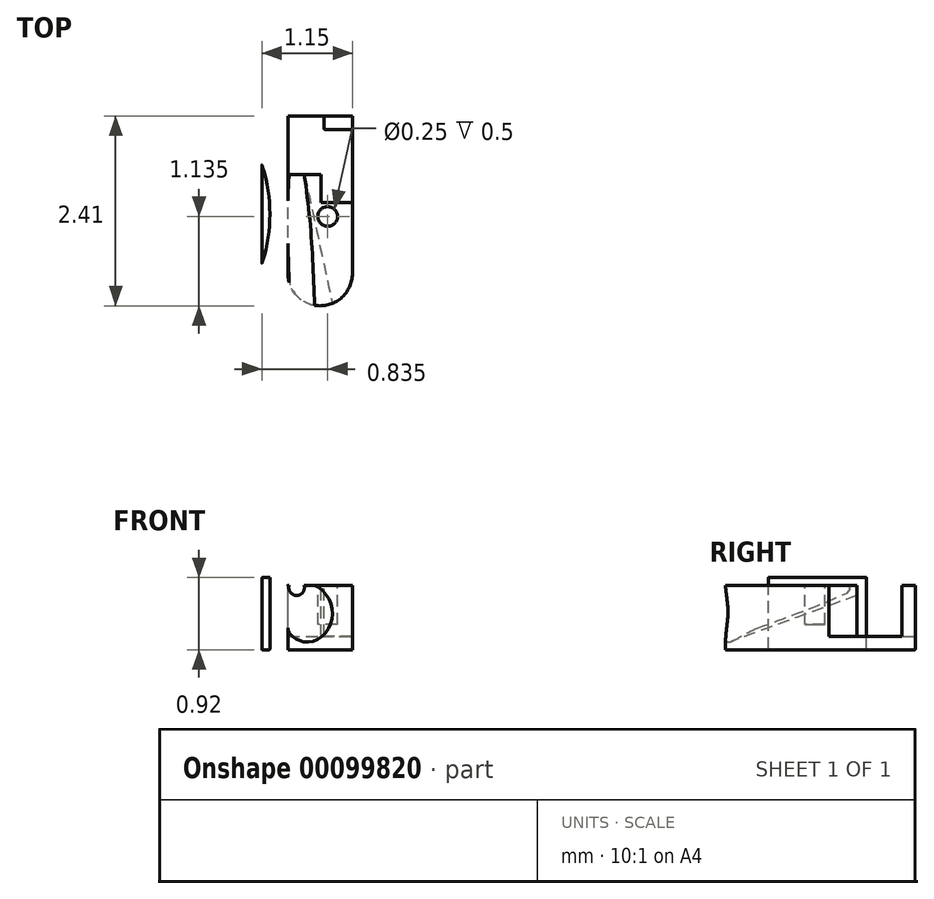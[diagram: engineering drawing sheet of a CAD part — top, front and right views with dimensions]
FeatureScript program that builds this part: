
annotation { "Feature Type Name" : "Feature", "Feature Type Description" : "" }
export const myFeature = defineFeature(function(context is Context, id is Id, definition is map)
    precondition{}
    {
        {
            var Q0;
            Q0=qCreatedBy(makeId("Front.planeOp"),FACE);
            var sketch = newSketch(context, id + "F0", { "sketchPlane" : qUnion([Q0])});
            skLineSegment(sketch, "E0", {"start": v(0, 0) * mm, "end": v(0.71, 0) * mm});
            skLineSegment(sketch, "E1", {"start": v(0.71, 0) * mm, "end": v(0.71, 0.92) * mm});
            skLineSegment(sketch, "E2", {"start": v(0.71, 0.92) * mm, "end": v(0, 0.92) * mm});
            skLineSegment(sketch, "E3.MirrorCS", {"start": v(-0.71, 0.92) * mm, "end": v(0, 0.92) * mm});
            skLineSegment(sketch, "E4.MirrorCS", {"start": v(-0.71, 0) * mm, "end": v(-0.71, 0.92) * mm});
            skLineSegment(sketch, "E5.MirrorCS", {"start": v(0, 0) * mm, "end": v(-0.71, 0) * mm});
            skSolve(sketch);
        }
        {
            var Q0;
            Q0 = qSketchRegion(id + "F0", true);
            var Q1;
            Q1=makeQuery(id+"F0.imprint","IMPRINT",FACE,{"disambiguationData":[TD([[makeQuery(id+"F0.imprint","IMPRINT",EDGE,{"derivedFrom":sQuery(id+"F0.wireOp",EDGE,"E0")}),1.0]])]});
            extrude(context, id + "F1", {"entities" : qUnion([Q0, Q1]), "oppositeDirection" : true, "depth" : 2.5 * mm});
        }
        {
            var Q0;
            Q0=qCreatedBy(makeId("Front.planeOp"),FACE);
            cPlane(context, id + "F2", {"entities" : qUnion([Q0]), "cplaneType" : CPlaneType.OFFSET, "offset" : 1.75 * mm, "oppositeDirection" : true, "width" : 150 * mm, "height" : 150 * mm});
        }
        {
            var Q0;
            Q0=qCreatedBy(id+"F2.planeOp",FACE);
            var sketch = newSketch(context, id + "F3", { "sketchPlane" : qUnion([Q0])});
            skCircle(sketch, "E6", {"center": v(-0.27, 0.79) * mm, "radius": 0.1 * mm});
            skSolve(sketch);
        }
        {
            var Q0;
            Q0=makeQuery(id+"F1.opExtrude","CAP_FACE",FACE,{"disambiguationData":[OSD([sQuery(id+"F0.wireOp",EDGE,"E0"),sQuery(id+"F0.wireOp",EDGE,"E1"),sQuery(id+"F0.wireOp",EDGE,"E2"),sQuery(id+"F0.wireOp",EDGE,"E3.MirrorCS"),sQuery(id+"F0.wireOp",EDGE,"E4.MirrorCS"),sQuery(id+"F0.wireOp",EDGE,"E5.MirrorCS")])],"isStart":true});
            var sketch = newSketch(context, id + "F4", { "sketchPlane" : qUnion([Q0])});
            skCircle(sketch, "E7", {"center": v(-0.2, 0.45) * mm, "radius": 0.4 * mm});
            skSolve(sketch);
        }
        {
            var Q1;
            Q1 = qSketchRegion(id + "F4", true);
            var Q2;
            Q2 = qSketchRegion(id + "F3", true);
            loft(context, id + "F5", {"operationType" : NewBodyOperationType.REMOVE, "sheetProfilesArray" : [{ "sheetProfileEntities" : qUnion([Q1]) }, { "sheetProfileEntities" : qUnion([Q2]) }]});
        }
        {
            var Q0;
            Q0=makeQuery(id+"F1.opExtrude","SWEPT_FACE",FACE,{"disambiguationData":[OSD([sQuery(id+"F0.wireOp",EDGE,"E2"),sQuery(id+"F0.wireOp",EDGE,"E3.MirrorCS")])]});
            var sketch = newSketch(context, id + "F6", { "sketchPlane" : qUnion([Q0])});
            skLineSegment(sketch, "E8", {"start": v(0.44, 2.5) * mm, "end": v(0.44, 0.49) * mm});
            skLineSegment(sketch, "E9", {"start": v(-0.38, 2.5) * mm, "end": v(-0.38, 0.49) * mm});
            skArc(sketch, "E10", {"start": v(-0.38, 0.49) * mm, "mid": v(0.03, 0.08) * mm, "end": v(0.44, 0.49) * mm});
            skLineSegment(sketch, "E11", {"start": v(-0.38, 2.5) * mm, "end": v(0.44, 2.5) * mm});
            skSolve(sketch);
        }
        {
            var Q0;
            Q0 = qSketchRegion(id + "F6", true);
            extrude(context, id + "F7", {"entities" : qUnion([Q0]), "operationType" : NewBodyOperationType.REMOVE, "oppositeDirection" : true, "depth" : 0.1 * mm});
        }
        {
            var Q0;
            Q0=makeQuery(id+"F7.boolean.opBoolean","COPY",FACE,{"derivedFrom":makeQuery(id+"F7.opExtrude","CAP_FACE",FACE,{"disambiguationData":[OSD([sQuery(id+"F6.wireOp",EDGE,"E8"),sQuery(id+"F6.wireOp",EDGE,"E9"),sQuery(id+"F6.wireOp",EDGE,"E10"),sQuery(id+"F6.wireOp",EDGE,"E11")])],"isStart":false})});
            var sketch = newSketch(context, id + "F8", { "sketchPlane" : qUnion([Q0])});
            skLineSegment(sketch, "E12", {"start": v(-0.38, 2.5) * mm, "end": v(0.08, 2.5) * mm});
            skLineSegment(sketch, "E13", {"start": v(-0.38, 1.75) * mm, "end": v(0.04, 1.75) * mm});
            skLineSegment(sketch, "E14", {"start": v(0.04, 1.75) * mm, "end": v(0.04, 1.4) * mm});
            skLineSegment(sketch, "E15", {"start": v(0.04, 1.4) * mm, "end": v(0.44, 1.4) * mm});
            skLineSegment(sketch, "E16", {"start": v(0.44, 1.4) * mm, "end": v(0.44, 2.32) * mm});
            skLineSegment(sketch, "E17", {"start": v(0.44, 2.32) * mm, "end": v(0.08, 2.32) * mm});
            skLineSegment(sketch, "E18", {"start": v(0.08, 2.32) * mm, "end": v(0.08, 2.5) * mm});
            skLineSegment(sketch, "E19", {"start": v(-0.38, 1.75) * mm, "end": v(-0.38, 2.5) * mm});
            skSolve(sketch);
        }
        {
            var Q0;
            Q0 = qSketchRegion(id + "F8", true);
            extrude(context, id + "F9", {"entities" : qUnion([Q0]), "operationType" : NewBodyOperationType.REMOVE, "oppositeDirection" : true, "depth" : 0.65 * mm});
        }
        {
            var Q0;
            Q0=makeQuery(id+"F1.opExtrude","SWEPT_FACE",FACE,{"disambiguationData":[OSD([sQuery(id+"F0.wireOp",EDGE,"E2"),sQuery(id+"F0.wireOp",EDGE,"E3.MirrorCS")])]});
            var sketch = newSketch(context, id + "F10", { "sketchPlane" : qUnion([Q0])});
            skLineSegment(sketch, "E20", {"start": v(0.71, 2.5) * mm, "end": v(0.71, 1.87) * mm});
            skLineSegment(sketch, "E21", {"start": v(0.71, 0) * mm, "end": v(0.71, 0.62) * mm});
            skLineSegment(sketch, "E22.MirrorCS", {"start": v(-0.71, 2.5) * mm, "end": v(-0.7, 1.87) * mm});
            skLineSegment(sketch, "E23.MirrorCS", {"start": v(-0.71, 0) * mm, "end": v(-0.71, 0.62) * mm});
            skArc(sketch, "E24", {"start": v(0.7, 1.87) * mm, "mid": v(0.6, 1.24) * mm, "end": v(0.7, 0.62) * mm});
            skArc(sketch, "E25.MirrorCS", {"start": v(-0.7, 1.87) * mm, "mid": v(-0.6, 1.24) * mm, "end": v(-0.7, 0.62) * mm});
            skLineSegment(sketch, "E26", {"start": v(0.71, 1.87) * mm, "end": v(0.71, 0.62) * mm});
            skLineSegment(sketch, "E27", {"start": v(-0.71, 1.87) * mm, "end": v(-0.71, 0.62) * mm});
            skSolve(sketch);
        }
        {
            var Q0;
            Q0=makeQuery(id+"F10.imprint","IMPRINT",FACE,{"disambiguationData":[TD([[makeQuery(id+"F10.imprint","IMPRINT",EDGE,{"derivedFrom":sQuery(id+"F10.wireOp",EDGE,"E24")}),1.0]])]});
            var Q1;
            Q1=makeQuery(id+"F10.imprint","IMPRINT",FACE,{"disambiguationData":[TD([[makeQuery(id+"F10.imprint","IMPRINT",EDGE,{"derivedFrom":sQuery(id+"F10.wireOp",EDGE,"E25.MirrorCS")}),-1.0]])]});
            extrude(context, id + "F11", {"entities" : qUnion([Q0, Q1]), "operationType" : NewBodyOperationType.REMOVE, "oppositeDirection" : true, "depth" : 25 * mm});
        }
        {
            var Q0;
            {var subQ0=sQuery(id+"F6.wireOp",EDGE,"E10");var subQ1=sQuery(id+"F6.wireOp",EDGE,"E8");Q0=makeQuery(id+"F9.boolean.opBoolean","SPLIT",FACE,{"disambiguationData":[TD([makeQuery(id+"F9.opExtrude","SWEPT_FACE",FACE,{"disambiguationData":[OSD([sQuery(id+"F8.wireOp",EDGE,"E14")])]})])],"derivedFrom":makeQuery(id+"F7.boolean.opBoolean","COPY",FACE,{"derivedFrom":makeQuery(id+"F7.opExtrude","CAP_FACE",FACE,{"disambiguationData":[OSD([subQ1,sQuery(id+"F6.wireOp",EDGE,"E9"),subQ0,sQuery(id+"F6.wireOp",EDGE,"E11")])],"isStart":false})})});}
            var sketch = newSketch(context, id + "F12", { "sketchPlane" : qUnion([Q0])});
            skCircle(sketch, "E28", {"center": v(0.12, 1.21) * mm, "radius": 0.12 * mm});
            skSolve(sketch);
        }
        {
            var Q0;
            Q0=makeQuery(id+"F12.imprint","IMPRINT",FACE,{"disambiguationData":[TD([[makeQuery(id+"F12.imprint","IMPRINT",EDGE,{"derivedFrom":sQuery(id+"F12.wireOp",EDGE,"E28")}),1.0]])]});
            extrude(context, id + "F13", {"entities" : qUnion([Q0]), "operationType" : NewBodyOperationType.REMOVE, "oppositeDirection" : true, "depth" : 0.5 * mm});
        }
        {
            var Q0;
            Q0=makeQuery(id+"F1.opExtrude","CAP_EDGE",EDGE,{"disambiguationData":[OSD([sQuery(id+"F0.wireOp",EDGE,"E1")])],"isStart":true});
            var Q1;
            Q1=makeQuery(id+"F1.opExtrude","CAP_EDGE",EDGE,{"disambiguationData":[OSD([sQuery(id+"F0.wireOp",EDGE,"E4.MirrorCS")])],"isStart":true});
            var Q2;
            Q2=makeQuery(id+"F1.opExtrude","CAP_EDGE",EDGE,{"disambiguationData":[OSD([sQuery(id+"F0.wireOp",EDGE,"E4.MirrorCS")])],"isStart":false});
            var Q3;
            Q3=makeQuery(id+"F1.opExtrude","CAP_EDGE",EDGE,{"disambiguationData":[OSD([sQuery(id+"F0.wireOp",EDGE,"E1")])],"isStart":false});
            var Q4;
            {var subQ0=sQuery(id+"F0.wireOp",EDGE,"E4.MirrorCS");var subQ1=sQuery(id+"F0.wireOp",EDGE,"E3.MirrorCS");var subQ2=sQuery(id+"F0.wireOp",EDGE,"E2");Q4=makeQuery(id+"F11.boolean.opBoolean","SPLIT",EDGE,{"disambiguationData":[TD([makeQuery(id+"F1.opExtrude","CAP_FACE",FACE,{"disambiguationData":[OSD([sQuery(id+"F0.wireOp",EDGE,"E0"),sQuery(id+"F0.wireOp",EDGE,"E1"),subQ2,subQ1,subQ0,sQuery(id+"F0.wireOp",EDGE,"E5.MirrorCS")])],"isStart":true})])],"derivedFrom":makeQuery(id+"F1.opExtrude","SWEPT_EDGE",EDGE,{"disambiguationData":[OSD([subQ1,subQ0])]})});}
            var Q5;
            Q5=makeQuery(id+"F11.boolean.opBoolean","COPY",EDGE,{"derivedFrom":makeQuery(id+"F11.opExtrude","CAP_EDGE",EDGE,{"disambiguationData":[OSD([sQuery(id+"F10.wireOp",EDGE,"E25.MirrorCS")])],"isStart":true})});
            var Q6;
            {var subQ0=sQuery(id+"F0.wireOp",EDGE,"E4.MirrorCS");var subQ1=sQuery(id+"F0.wireOp",EDGE,"E3.MirrorCS");var subQ2=sQuery(id+"F0.wireOp",EDGE,"E2");Q6=makeQuery(id+"F11.boolean.opBoolean","SPLIT",EDGE,{"disambiguationData":[TD([makeQuery(id+"F1.opExtrude","CAP_FACE",FACE,{"disambiguationData":[OSD([sQuery(id+"F0.wireOp",EDGE,"E0"),sQuery(id+"F0.wireOp",EDGE,"E1"),subQ2,subQ1,subQ0,sQuery(id+"F0.wireOp",EDGE,"E5.MirrorCS")])],"isStart":false})])],"derivedFrom":makeQuery(id+"F1.opExtrude","SWEPT_EDGE",EDGE,{"disambiguationData":[OSD([subQ1,subQ0])]})});}
            var Q7;
            {var subQ0=sQuery(id+"F0.wireOp",EDGE,"E4.MirrorCS");var subQ1=sQuery(id+"F0.wireOp",EDGE,"E3.MirrorCS");var subQ2=sQuery(id+"F0.wireOp",EDGE,"E2");Q7=makeQuery(id+"F7.boolean.opBoolean","SPLIT",EDGE,{"disambiguationData":[TD([makeQuery(id+"F1.opExtrude","SWEPT_FACE",FACE,{"disambiguationData":[OSD([subQ0])]})])],"derivedFrom":makeQuery(id+"F1.opExtrude","CAP_EDGE",EDGE,{"disambiguationData":[OSD([subQ2,subQ1])],"isStart":false})});}
            var Q8;
            Q8=makeQuery(id+"F7.boolean.opBoolean","COPY",EDGE,{"derivedFrom":makeQuery(id+"F7.opExtrude","CAP_EDGE",EDGE,{"disambiguationData":[OSD([sQuery(id+"F6.wireOp",EDGE,"E9")])],"isStart":true})});
            var Q9;
            Q9=makeQuery(id+"F7.boolean.opBoolean","COPY",EDGE,{"derivedFrom":makeQuery(id+"F7.opExtrude","CAP_EDGE",EDGE,{"disambiguationData":[OSD([sQuery(id+"F6.wireOp",EDGE,"E10")])],"isStart":true})});
            var Q10;
            Q10=makeQuery(id+"F7.boolean.opBoolean","COPY",EDGE,{"derivedFrom":makeQuery(id+"F7.opExtrude","CAP_EDGE",EDGE,{"disambiguationData":[OSD([sQuery(id+"F6.wireOp",EDGE,"E8")])],"isStart":true})});
            var Q11;
            {var subQ0=sQuery(id+"F0.wireOp",EDGE,"E3.MirrorCS");var subQ1=sQuery(id+"F0.wireOp",EDGE,"E2");var subQ2=sQuery(id+"F0.wireOp",EDGE,"E1");Q11=makeQuery(id+"F7.boolean.opBoolean","SPLIT",EDGE,{"disambiguationData":[TD([makeQuery(id+"F1.opExtrude","SWEPT_FACE",FACE,{"disambiguationData":[OSD([subQ2])]})])],"derivedFrom":makeQuery(id+"F1.opExtrude","CAP_EDGE",EDGE,{"disambiguationData":[OSD([subQ1,subQ0])],"isStart":false})});}
            var Q12;
            {var subQ0=sQuery(id+"F0.wireOp",EDGE,"E3.MirrorCS");var subQ1=sQuery(id+"F0.wireOp",EDGE,"E2");var subQ2=sQuery(id+"F0.wireOp",EDGE,"E1");Q12=makeQuery(id+"F11.boolean.opBoolean","SPLIT",EDGE,{"disambiguationData":[TD([makeQuery(id+"F1.opExtrude","CAP_FACE",FACE,{"disambiguationData":[OSD([sQuery(id+"F0.wireOp",EDGE,"E0"),subQ2,subQ1,subQ0,sQuery(id+"F0.wireOp",EDGE,"E4.MirrorCS"),sQuery(id+"F0.wireOp",EDGE,"E5.MirrorCS")])],"isStart":false})])],"derivedFrom":makeQuery(id+"F1.opExtrude","SWEPT_EDGE",EDGE,{"disambiguationData":[OSD([subQ2,subQ1])]})});}
            var Q13;
            Q13=makeQuery(id+"F11.boolean.opBoolean","COPY",EDGE,{"derivedFrom":makeQuery(id+"F11.opExtrude","CAP_EDGE",EDGE,{"disambiguationData":[OSD([sQuery(id+"F10.wireOp",EDGE,"E24")])],"isStart":true})});
            var Q14;
            {var subQ0=sQuery(id+"F0.wireOp",EDGE,"E3.MirrorCS");var subQ1=sQuery(id+"F0.wireOp",EDGE,"E2");var subQ2=sQuery(id+"F0.wireOp",EDGE,"E1");Q14=makeQuery(id+"F11.boolean.opBoolean","SPLIT",EDGE,{"disambiguationData":[TD([makeQuery(id+"F1.opExtrude","CAP_FACE",FACE,{"disambiguationData":[OSD([sQuery(id+"F0.wireOp",EDGE,"E0"),subQ2,subQ1,subQ0,sQuery(id+"F0.wireOp",EDGE,"E4.MirrorCS"),sQuery(id+"F0.wireOp",EDGE,"E5.MirrorCS")])],"isStart":true})])],"derivedFrom":makeQuery(id+"F1.opExtrude","SWEPT_EDGE",EDGE,{"disambiguationData":[OSD([subQ2,subQ1])]})});}
            var Q15;
            Q15=makeQuery(id+"F1.opExtrude","CAP_EDGE",EDGE,{"disambiguationData":[OSD([sQuery(id+"F0.wireOp",EDGE,"E2"),sQuery(id+"F0.wireOp",EDGE,"E3.MirrorCS")])],"isStart":true});
            var Q16;
            Q16=makeQuery(id+"F1.opExtrude","CAP_EDGE",EDGE,{"disambiguationData":[OSD([sQuery(id+"F0.wireOp",EDGE,"E0"),sQuery(id+"F0.wireOp",EDGE,"E5.MirrorCS")])],"isStart":true});
            var Q17;
            {var subQ0=sQuery(id+"F0.wireOp",EDGE,"E5.MirrorCS");var subQ1=sQuery(id+"F0.wireOp",EDGE,"E4.MirrorCS");var subQ2=sQuery(id+"F0.wireOp",EDGE,"E0");Q17=makeQuery(id+"F11.boolean.opBoolean","SPLIT",EDGE,{"disambiguationData":[TD([makeQuery(id+"F1.opExtrude","CAP_FACE",FACE,{"disambiguationData":[OSD([subQ2,sQuery(id+"F0.wireOp",EDGE,"E1"),sQuery(id+"F0.wireOp",EDGE,"E2"),sQuery(id+"F0.wireOp",EDGE,"E3.MirrorCS"),subQ1,subQ0])],"isStart":false})])],"derivedFrom":makeQuery(id+"F1.opExtrude","SWEPT_EDGE",EDGE,{"disambiguationData":[OSD([subQ1,subQ0])]})});}
            var Q18;
            Q18=makeQuery(id+"F11.boolean.opBoolean","INTERSECT",EDGE,{"derivedFrom":[makeQuery(id+"F1.opExtrude","SWEPT_FACE",FACE,{"disambiguationData":[OSD([sQuery(id+"F0.wireOp",EDGE,"E0"),sQuery(id+"F0.wireOp",EDGE,"E5.MirrorCS")])]}),makeQuery(id+"F11.opExtrude","SWEPT_FACE",FACE,{"disambiguationData":[OSD([sQuery(id+"F10.wireOp",EDGE,"E25.MirrorCS")])]})]});
            var Q19;
            {var subQ0=sQuery(id+"F0.wireOp",EDGE,"E5.MirrorCS");var subQ1=sQuery(id+"F0.wireOp",EDGE,"E4.MirrorCS");var subQ2=sQuery(id+"F0.wireOp",EDGE,"E0");Q19=makeQuery(id+"F11.boolean.opBoolean","SPLIT",EDGE,{"disambiguationData":[TD([makeQuery(id+"F1.opExtrude","CAP_FACE",FACE,{"disambiguationData":[OSD([subQ2,sQuery(id+"F0.wireOp",EDGE,"E1"),sQuery(id+"F0.wireOp",EDGE,"E2"),sQuery(id+"F0.wireOp",EDGE,"E3.MirrorCS"),subQ1,subQ0])],"isStart":true})])],"derivedFrom":makeQuery(id+"F1.opExtrude","SWEPT_EDGE",EDGE,{"disambiguationData":[OSD([subQ1,subQ0])]})});}
            var Q20;
            Q20=makeQuery(id+"F11.boolean.opBoolean","COPY",EDGE,{"derivedFrom":makeQuery(id+"F11.opExtrude","SWEPT_EDGE",EDGE,{"disambiguationData":[OSD([sQuery(id+"F10.wireOp",EDGE,"E23.MirrorCS"),sQuery(id+"F10.wireOp",EDGE,"E25.MirrorCS"),sQuery(id+"F10.wireOp",EDGE,"E27")])]})});
            var Q21;
            Q21=makeQuery(id+"F11.boolean.opBoolean","COPY",EDGE,{"derivedFrom":makeQuery(id+"F11.opExtrude","SWEPT_EDGE",EDGE,{"disambiguationData":[OSD([sQuery(id+"F10.wireOp",EDGE,"E22.MirrorCS"),sQuery(id+"F10.wireOp",EDGE,"E25.MirrorCS"),sQuery(id+"F10.wireOp",EDGE,"E27")])]})});
            var Q22;
            Q22=makeQuery(id+"F11.boolean.opBoolean","COPY",EDGE,{"derivedFrom":makeQuery(id+"F11.opExtrude","SWEPT_EDGE",EDGE,{"disambiguationData":[OSD([sQuery(id+"F10.wireOp",EDGE,"E20"),sQuery(id+"F10.wireOp",EDGE,"E24"),sQuery(id+"F10.wireOp",EDGE,"E26")])]})});
            var Q23;
            Q23=makeQuery(id+"F11.boolean.opBoolean","COPY",EDGE,{"derivedFrom":makeQuery(id+"F11.opExtrude","SWEPT_EDGE",EDGE,{"disambiguationData":[OSD([sQuery(id+"F10.wireOp",EDGE,"E21"),sQuery(id+"F10.wireOp",EDGE,"E24"),sQuery(id+"F10.wireOp",EDGE,"E26")])]})});
            var Q24;
            {var subQ0=sQuery(id+"F0.wireOp",EDGE,"E5.MirrorCS");var subQ1=sQuery(id+"F0.wireOp",EDGE,"E1");var subQ2=sQuery(id+"F0.wireOp",EDGE,"E0");Q24=makeQuery(id+"F11.boolean.opBoolean","SPLIT",EDGE,{"disambiguationData":[TD([makeQuery(id+"F1.opExtrude","CAP_FACE",FACE,{"disambiguationData":[OSD([subQ2,subQ1,sQuery(id+"F0.wireOp",EDGE,"E2"),sQuery(id+"F0.wireOp",EDGE,"E3.MirrorCS"),sQuery(id+"F0.wireOp",EDGE,"E4.MirrorCS"),subQ0])],"isStart":false})])],"derivedFrom":makeQuery(id+"F1.opExtrude","SWEPT_EDGE",EDGE,{"disambiguationData":[OSD([subQ2,subQ1])]})});}
            var Q25;
            Q25=makeQuery(id+"F11.boolean.opBoolean","INTERSECT",EDGE,{"derivedFrom":[makeQuery(id+"F1.opExtrude","SWEPT_FACE",FACE,{"disambiguationData":[OSD([sQuery(id+"F0.wireOp",EDGE,"E0"),sQuery(id+"F0.wireOp",EDGE,"E5.MirrorCS")])]}),makeQuery(id+"F11.opExtrude","SWEPT_FACE",FACE,{"disambiguationData":[OSD([sQuery(id+"F10.wireOp",EDGE,"E24")])]})]});
            var Q26;
            {var subQ0=sQuery(id+"F0.wireOp",EDGE,"E5.MirrorCS");var subQ1=sQuery(id+"F0.wireOp",EDGE,"E1");var subQ2=sQuery(id+"F0.wireOp",EDGE,"E0");Q26=makeQuery(id+"F11.boolean.opBoolean","SPLIT",EDGE,{"disambiguationData":[TD([makeQuery(id+"F1.opExtrude","CAP_FACE",FACE,{"disambiguationData":[OSD([subQ2,subQ1,sQuery(id+"F0.wireOp",EDGE,"E2"),sQuery(id+"F0.wireOp",EDGE,"E3.MirrorCS"),sQuery(id+"F0.wireOp",EDGE,"E4.MirrorCS"),subQ0])],"isStart":true})])],"derivedFrom":makeQuery(id+"F1.opExtrude","SWEPT_EDGE",EDGE,{"disambiguationData":[OSD([subQ2,subQ1])]})});}
            var Q27;
            Q27=makeQuery(id+"F1.opExtrude","CAP_EDGE",EDGE,{"disambiguationData":[OSD([sQuery(id+"F0.wireOp",EDGE,"E0"),sQuery(id+"F0.wireOp",EDGE,"E5.MirrorCS")])],"isStart":false});
            var Q28;
            Q28=makeQuery(id+"F7.boolean.opBoolean","COPY",EDGE,{"derivedFrom":makeQuery(id+"F7.opExtrude","SWEPT_EDGE",EDGE,{"disambiguationData":[OSD([sQuery(id+"F0.wireOp",EDGE,"E2"),sQuery(id+"F0.wireOp",EDGE,"E3.MirrorCS"),sQuery(id+"F6.wireOp",EDGE,"E8"),sQuery(id+"F6.wireOp",EDGE,"E11")])]})});
            var Q29;
            Q29=makeQuery(id+"F7.boolean.opBoolean","COPY",EDGE,{"derivedFrom":makeQuery(id+"F7.opExtrude","CAP_EDGE",EDGE,{"disambiguationData":[OSD([sQuery(id+"F6.wireOp",EDGE,"E11")])],"isStart":false})});
            var Q30;
            Q30=makeQuery(id+"F9.boolean.opBoolean","COPY",EDGE,{"derivedFrom":makeQuery(id+"F9.opExtrude","SWEPT_EDGE",EDGE,{"disambiguationData":[OSD([sQuery(id+"F6.wireOp",EDGE,"E11"),sQuery(id+"F8.wireOp",EDGE,"E12"),sQuery(id+"F8.wireOp",EDGE,"E18")])]})});
            var Q31;
            Q31=makeQuery(id+"F9.boolean.opBoolean","COPY",EDGE,{"derivedFrom":makeQuery(id+"F9.opExtrude","CAP_EDGE",EDGE,{"disambiguationData":[OSD([sQuery(id+"F8.wireOp",EDGE,"E12")])],"isStart":false})});
            var Q32;
            Q32=makeQuery(id+"F9.boolean.opBoolean","MERGE",EDGE,{"derivedFrom":[makeQuery(id+"F7.boolean.opBoolean","COPY",EDGE,{"derivedFrom":makeQuery(id+"F7.opExtrude","SWEPT_EDGE",EDGE,{"disambiguationData":[OSD([sQuery(id+"F0.wireOp",EDGE,"E2"),sQuery(id+"F0.wireOp",EDGE,"E3.MirrorCS"),sQuery(id+"F6.wireOp",EDGE,"E9"),sQuery(id+"F6.wireOp",EDGE,"E11")])]})}),makeQuery(id+"F9.opExtrude","SWEPT_EDGE",EDGE,{"disambiguationData":[OSD([sQuery(id+"F8.wireOp",EDGE,"E12"),sQuery(id+"F8.wireOp",EDGE,"E19")])]})]});
            var Q33;
            Q33=makeQuery(id+"F9.boolean.opBoolean","COPY",EDGE,{"derivedFrom":makeQuery(id+"F9.opExtrude","SWEPT_EDGE",EDGE,{"disambiguationData":[OSD([sQuery(id+"F8.wireOp",EDGE,"E17"),sQuery(id+"F8.wireOp",EDGE,"E18")])]})});
            var Q34;
            Q34=makeQuery(id+"F9.boolean.opBoolean","COPY",EDGE,{"derivedFrom":makeQuery(id+"F9.opExtrude","CAP_EDGE",EDGE,{"disambiguationData":[OSD([sQuery(id+"F8.wireOp",EDGE,"E18")])],"isStart":true})});
            var Q35;
            Q35=makeQuery(id+"F9.boolean.opBoolean","COPY",EDGE,{"derivedFrom":makeQuery(id+"F9.opExtrude","CAP_EDGE",EDGE,{"disambiguationData":[OSD([sQuery(id+"F8.wireOp",EDGE,"E17")])],"isStart":true})});
            fillet(context, id + "F14", {"entities" : qUnion([Q0, Q1, Q2, Q3, Q4, Q5, Q6, Q7, Q8, Q9, Q10, Q11, Q12, Q13, Q14, Q15, Q16, Q17, Q18, Q19, Q20, Q21, Q22, Q23, Q24, Q25, Q26, Q27, Q28, Q29, Q30, Q31, Q32, Q33, Q34, Q35]), "radius" : 0.01 * mm, "tangentPropagation" : true, "allowEdgeOverflow" : false});
        }
    });
